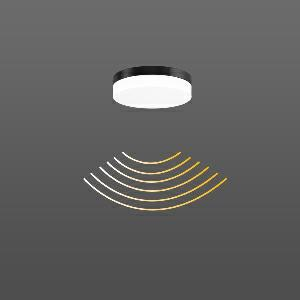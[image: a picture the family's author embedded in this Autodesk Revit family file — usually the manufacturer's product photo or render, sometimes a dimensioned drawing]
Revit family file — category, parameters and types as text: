
# Revit family: flat_slim_round_312135_0031_1_191_e418
name_source: partatom
category: Lighting Fixtures
units: mm (PartAtom-declared; Revit-internal decimal feet)

## family parameters
Cut with Voids When Loaded = No
Host = Face
Light Source = No
Part Type = Normal
Room Calculation Point = No
Round Connector Dimension = Use Diameter
Shared = No

## types (1)
- FLAT SLIM round (1 x LED Modul 840, 1100 lm, 4000)
    Apparent Load = 13 VA
    CIE Flux Codes = 43 74 92 91 100
    Color Rendering = 80
    Color Temperature = 4000
    Default Elevation = 1800 mm
    Height = 63 mm
    Lamp = 1 x LED Modul 840
    Lamp Light Flux = 1100 lm
    Lamp count = 1
    Length = 230 mm
    Lifetime = 50000 h
    Luminous efficacy = 85 lm/W
    Manufacturer = RZB
    ModVariant = No
    Model = 312135.0031.1.191
    Mounting Place = Ceiling, Wall
    Mounting Type = Surface mounted
    Number of Poles = 1
    OnlyDefault = Yes
    Power Factor = 1
    Product Name = FLAT SLIM round
    Product group = Surface mounted ceiling and wall luminaires
    ProductGroupID = 305
    Protection Class = Protection class I
    Protection Degree = IP 65
    RLX_Detail_Level = 1
    RLX_Emergency_Light_Flux = 0 lm
    RLX_Emergency_Type = 0
    RLX_Emergency_Type_DB = No
    RlxData = <blob elided: 31401 chars, md5=6aae8df0>
    Socket = socket
    Standby Power = 0 W
    System Light Flux = 1100 lm
    System Power = 13 W
    Type Comments = Product without accessories
    Type Image = 312132.0031.19.jpg
    URL = http://relux.com
    VarID = ---
    Voltage = 230 V
    Voltage Range = 220-240 V
    Weight = 0.00 kg
    Width = 0 mm  [stored 0 ft]

note: [stored X ft] marks values corroborated as IEEE doubles in the binary element streams (Revit-internal decimal feet)

## geometry (parser evidence)
native form markers: Blend x4, Sweep x12
no freeform markers — native parametric forms only
